# Revit family: DTD-21XA-I_Detector termovelocimétrico
name_source: partatom
category: Dispositivos de alarma de incendios
revit_build: Autodesk Revit 2017 (Build: 20190508_0315(x64)
units: mm (PartAtom-declared; Revit-internal decimal feet)

## family parameters
Anfitrión = Cara
Compartido = No
Corte con vacíos al cargar = No
Cota de conector redondo = Diámetro de uso
Mantener orientación de anotación = No
Punto de cálculo de habitación = No
Tipo de pieza = Normal

## types (2) — shared parameters
Altura = 100 mm
Anchura = 100 mm
Carga eléctrica = Otro
Conexionado = 2 x 1,5 mm² trenzado y apantallado conexión a base Z-200
Consumo en alarma = < 11 mA
Consumo en reposo = < 300 μA
Cuerpo = ABS
Elevación por defecto = 1219 mm
Fabricante = Detnov Security
Fases = 1
Humedad relativa = 95% sin condensación
Imagen de tipo = <Ninguno>
Potencia total = 0 VA
Profundidad = 40 mm
Teléfono = (+34) 93 371 60 25
Temperatura trabajo = De -10ºC a 70ºC
Tensión de trabajo = De 22 a 38VDC
URL = https://www.detnov.com
Voltaje = 230 V
Índice IP = IP20

## per-type parameters (varying)
| type | Certificación | Comentarios de tipo | Código de montaje | Descripción | Modelo |
| DTD-210A-I | EN 54-5 y EN 54-17 (DTD-210A solo EN 54-5) | Los detectores DTD-210A y DTD-210A-I están indicados para aquellas instalaciones de protección contra incendios en establecimientos donde un incendio provocaría más calor que humo, también esta indicado para aquellos establecimientos que exista humo, vapor o polvo de forma habitual dada su actividad , tales como cocinas industriales, salas de calderas, vestuarios y aparcamientos. | PDETDTD-210A-I | Detector termovelocimétrico (58ºC-8ºC/minuto) con aislador incorporado para sistema analógico, incorpora algoritmos de verificación. Marca Detnov, modelo DTD-210A-I. Led indicador de estado y salida para piloto remoto o zumbador, sistema anti hurto. Color blanco. Precisa zócalo de conexión Z-200 o Z-200-H. Certificados CPR EN54-5 y EN54-17. Dimensiones: 100 x 40 mm. | Detector DTD-210A-I |
| DTD-215A-I | EN 54-5 y EN 54-17 (DTD-215A solo EN 54-5) | El detector de incendios de Detnov ha sido desarrollado para asegurar una rápida reacción a los incendios, cumpliendo los máximos estándares de calidad y certificación requeridos en el mercado. Una fiabilidad única a la hora de detectar y proteger las instalaciones para reducir las falsas alarmas, siendo apropiados para las aplicaciones más exigentes. | PDETDTD-215A-I | Detector de alta temperatura (78ºC) con aislador incorporado para sistema analógico, incorpora algoritmos de verificación. Marca Detnov, modelo DTD-215A-I. Led indicador de estado y salida para piloto remoto o zumbador, sistema anti hurto. Color blanco. Precisa base de conexión Z-200 o Z-200-H. Certificados CPR EN54-5 y EN54-17. Dimensiones: 100 x 40 mm. | Detector DTD-215A-I |
